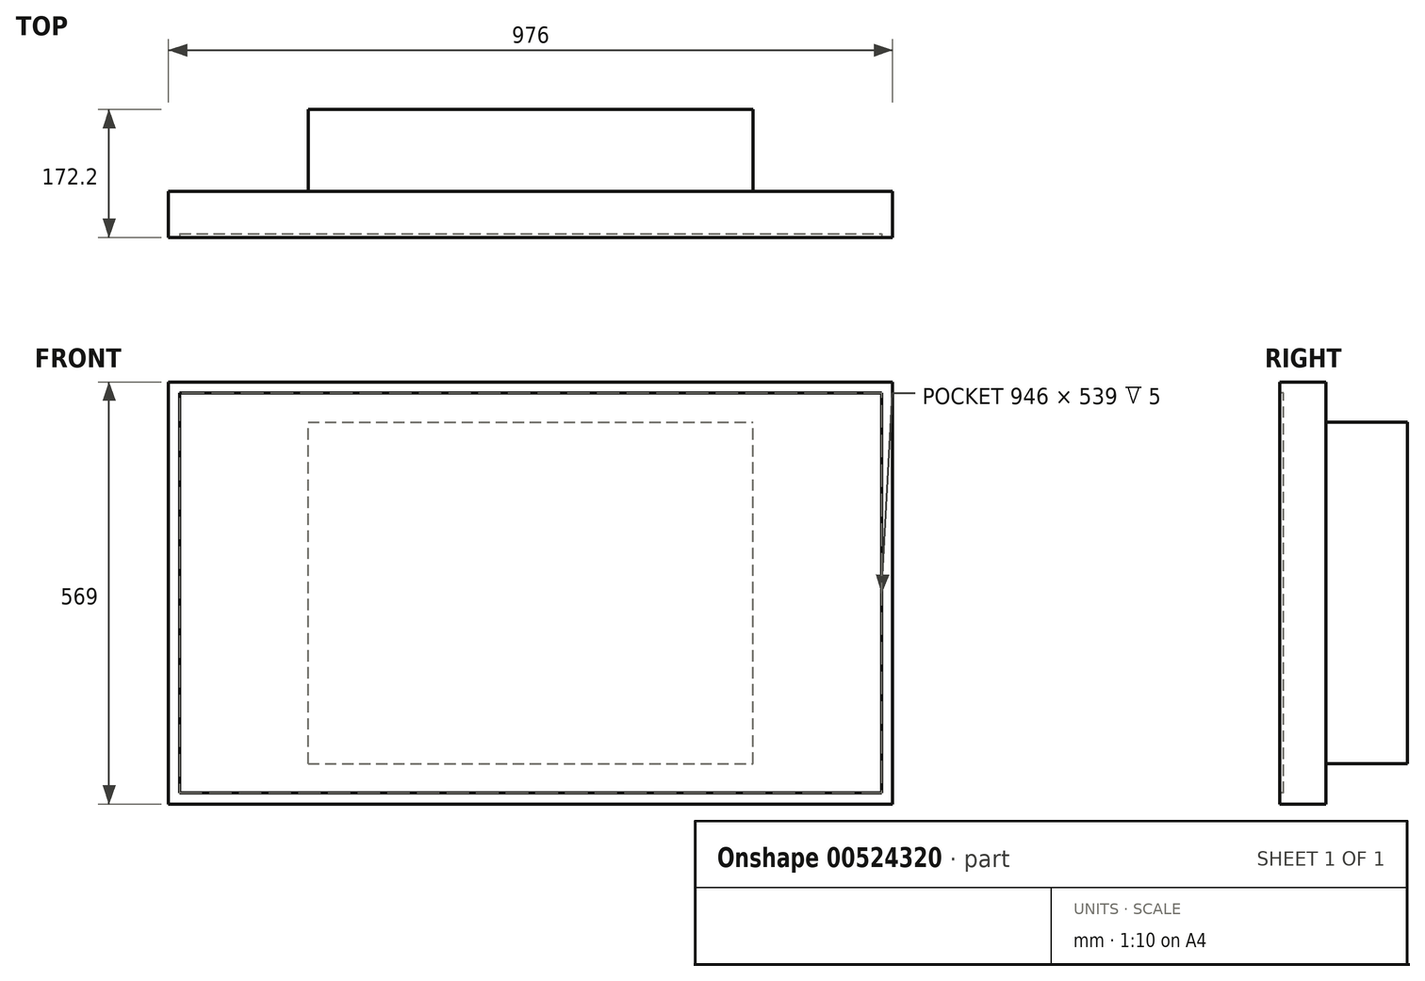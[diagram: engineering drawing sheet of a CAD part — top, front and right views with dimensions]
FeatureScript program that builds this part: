
annotation { "Feature Type Name" : "Feature", "Feature Type Description" : "" }
export const myFeature = defineFeature(function(context is Context, id is Id, definition is map)
    precondition{}
    {
        {
            var Q0;
            Q0=qCreatedBy(makeId("Front.planeOp"),FACE);
            var sketch = newSketch(context, id + "F0", { "sketchPlane" : qUnion([Q0])});
            skLineSegment(sketch, "E0.bottom", {"start": v(488, -284.5) * mm, "end": v(-488, -284.5) * mm});
            skLineSegment(sketch, "E0.top", {"start": v(488, 284.5) * mm, "end": v(-488, 284.5) * mm});
            skLineSegment(sketch, "E0.left", {"start": v(488, -284.5) * mm, "end": v(488, 284.5) * mm});
            skLineSegment(sketch, "E0.right", {"start": v(-488, -284.5) * mm, "end": v(-488, 284.5) * mm});
            skPoint(sketch, "E0.middle", {"position": v(0, 0) * mm});
            skSolve(sketch);
        }
        {
            var Q0;
            Q0=makeQuery(id+"F0.imprint","IMPRINT",FACE,{"disambiguationData":[TD([[makeQuery(id+"F0.imprint","IMPRINT",EDGE,{"derivedFrom":sQuery(id+"F0.wireOp",EDGE,"E0.bottom")}),-1.0]])]});
            extrude(context, id + "F1", {"entities" : qUnion([Q0]), "depth" : 62.2 * mm, "offsetDistance" : 25 * mm});
        }
        {
            var Q0;
            Q0=makeQuery(id+"F1.opExtrude","CAP_FACE",FACE,{"disambiguationData":[OSD([sQuery(id+"F0.wireOp",EDGE,"E0.bottom"),sQuery(id+"F0.wireOp",EDGE,"E0.top"),sQuery(id+"F0.wireOp",EDGE,"E0.left"),sQuery(id+"F0.wireOp",EDGE,"E0.right")])],"isStart":false});
            var sketch = newSketch(context, id + "F2", { "sketchPlane" : qUnion([Q0])});
            skLineSegment(sketch, "E1.0", {"start": v(473, -269.5) * mm, "end": v(473, 269.5) * mm});
            skLineSegment(sketch, "E1.1", {"start": v(-473, -269.5) * mm, "end": v(473, -269.5) * mm});
            skLineSegment(sketch, "E1.2", {"start": v(-473, 269.5) * mm, "end": v(-473, -269.5) * mm});
            skLineSegment(sketch, "E1.3", {"start": v(473, 269.5) * mm, "end": v(-473, 269.5) * mm});
            skSolve(sketch);
        }
        {
            var Q0;
            Q0 = qSketchRegion(id + "F2", true);
            extrude(context, id + "F3", {"entities" : qUnion([Q0]), "operationType" : NewBodyOperationType.REMOVE, "oppositeDirection" : true, "depth" : 5 * mm, "offsetDistance" : 25 * mm});
        }
        {
            var Q0;
            Q0=makeQuery(id+"F1.opExtrude","CAP_FACE",FACE,{"disambiguationData":[OSD([sQuery(id+"F0.wireOp",EDGE,"E0.bottom"),sQuery(id+"F0.wireOp",EDGE,"E0.top"),sQuery(id+"F0.wireOp",EDGE,"E0.left"),sQuery(id+"F0.wireOp",EDGE,"E0.right")])],"isStart":true});
            var sketch = newSketch(context, id + "F4", { "sketchPlane" : qUnion([Q0])});
            skLineSegment(sketch, "E2.bottom", {"start": v(300, -230) * mm, "end": v(-300, -230) * mm});
            skLineSegment(sketch, "E2.top", {"start": v(300, 230) * mm, "end": v(-300, 230) * mm});
            skLineSegment(sketch, "E2.left", {"start": v(300, -230) * mm, "end": v(300, 230) * mm});
            skLineSegment(sketch, "E2.right", {"start": v(-300, -230) * mm, "end": v(-300, 230) * mm});
            skPoint(sketch, "E2.middle", {"position": v(0, 0) * mm});
            skSolve(sketch);
        }
        {
            var Q0;
            Q0 = qSketchRegion(id + "F4", true);
            extrude(context, id + "F5", {"entities" : qUnion([Q0]), "depth" : 110 * mm, "offsetDistance" : 25 * mm});
        }
    });
